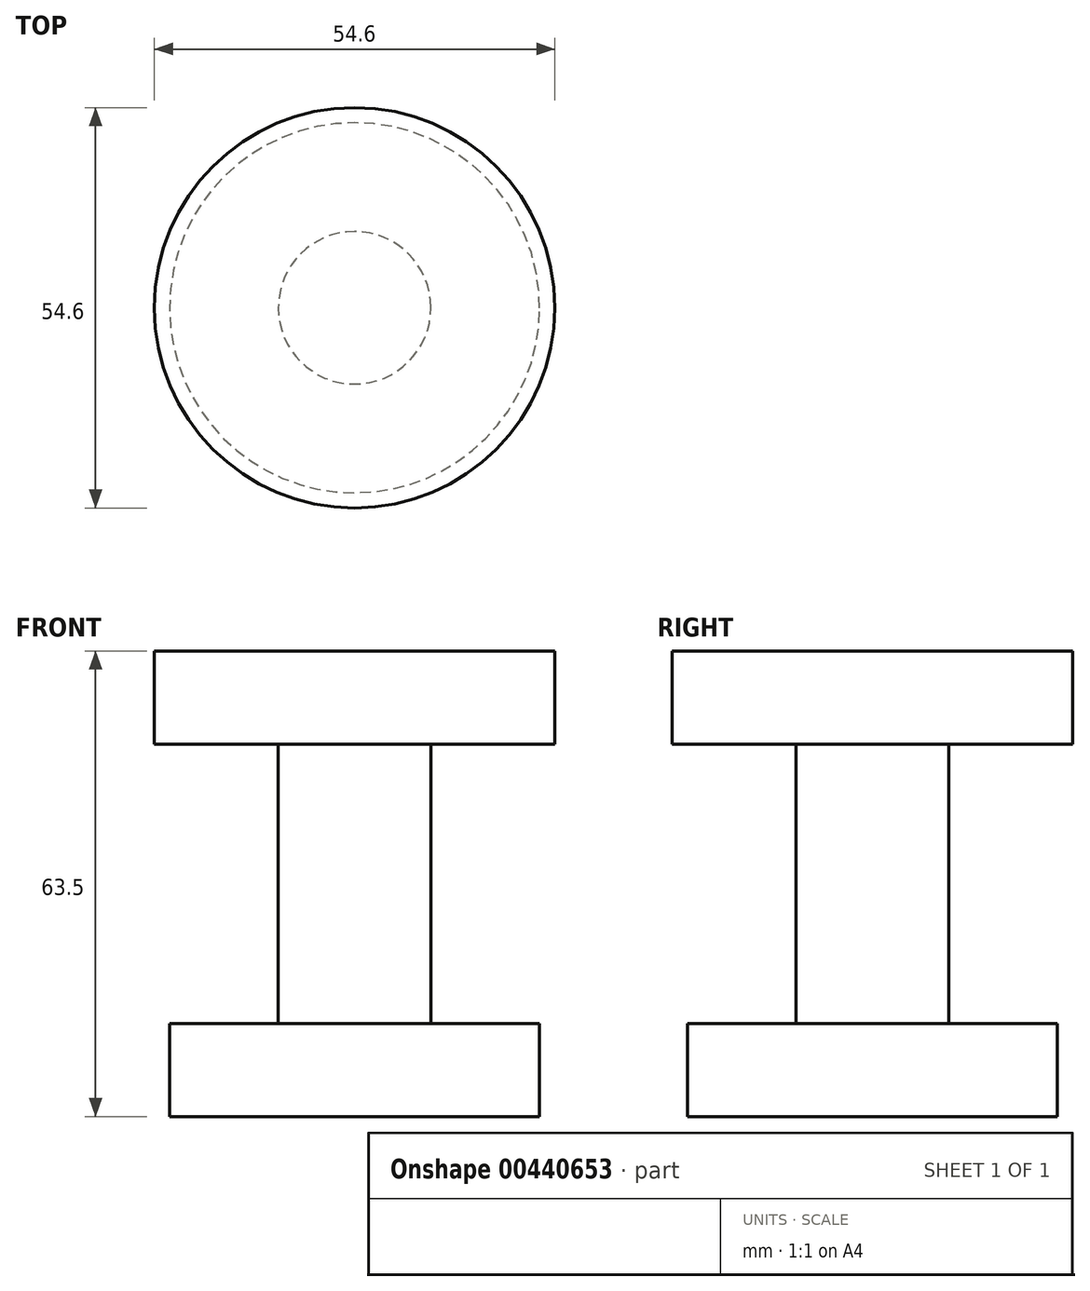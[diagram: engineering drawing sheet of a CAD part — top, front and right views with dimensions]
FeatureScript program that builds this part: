
annotation { "Feature Type Name" : "Feature", "Feature Type Description" : "" }
export const myFeature = defineFeature(function(context is Context, id is Id, definition is map)
    precondition{}
    {
        {
            var Q0;
            Q0=qCreatedBy(makeId("Top.planeOp"),FACE);
            var sketch = newSketch(context, id + "F0", { "sketchPlane" : qUnion([Q0])});
            skCircle(sketch, "E0", {"center": v(0, 0) * mm, "radius": 25.23 * mm});
            skSolve(sketch);
        }
        {
            var Q0;
            Q0 = qSketchRegion(id + "F0", true);
            extrude(context, id + "F1", {"entities" : qUnion([Q0]), "depth" : 12.7 * mm});
        }
        {
            var Q0;
            Q0=makeQuery(id+"F1.opExtrude","CAP_FACE",FACE,{"disambiguationData":[OSD([sQuery(id+"F0.wireOp",EDGE,"E0")])],"isStart":false});
            var sketch = newSketch(context, id + "F2", { "sketchPlane" : qUnion([Q0])});
            skCircle(sketch, "E1", {"center": v(0, 0) * mm, "radius": 10.4 * mm});
            skSolve(sketch);
        }
        {
            var Q0;
            Q0=makeQuery(id+"F2.imprint","IMPRINT",FACE,{"disambiguationData":[TD([[makeQuery(id+"F2.imprint","IMPRINT",EDGE,{"derivedFrom":sQuery(id+"F2.wireOp",EDGE,"E1")}),1.0]])]});
            extrude(context, id + "F3", {"entities" : qUnion([Q0]), "operationType" : NewBodyOperationType.ADD, "depth" : 38.1 * mm});
        }
        {
            var Q0;
            Q0=makeQuery(id+"F3.opExtrude","CAP_FACE",FACE,{"disambiguationData":[OSD([sQuery(id+"F2.wireOp",EDGE,"E1")])],"isStart":false});
            var sketch = newSketch(context, id + "F4", { "sketchPlane" : qUnion([Q0])});
            skCircle(sketch, "E2", {"center": v(0, 0) * mm, "radius": 27.3 * mm});
            skSolve(sketch);
        }
        {
            var Q0;
            Q0 = qSketchRegion(id + "F4", true);
            extrude(context, id + "F5", {"entities" : qUnion([Q0]), "operationType" : NewBodyOperationType.ADD, "depth" : 12.7 * mm});
        }
    });
